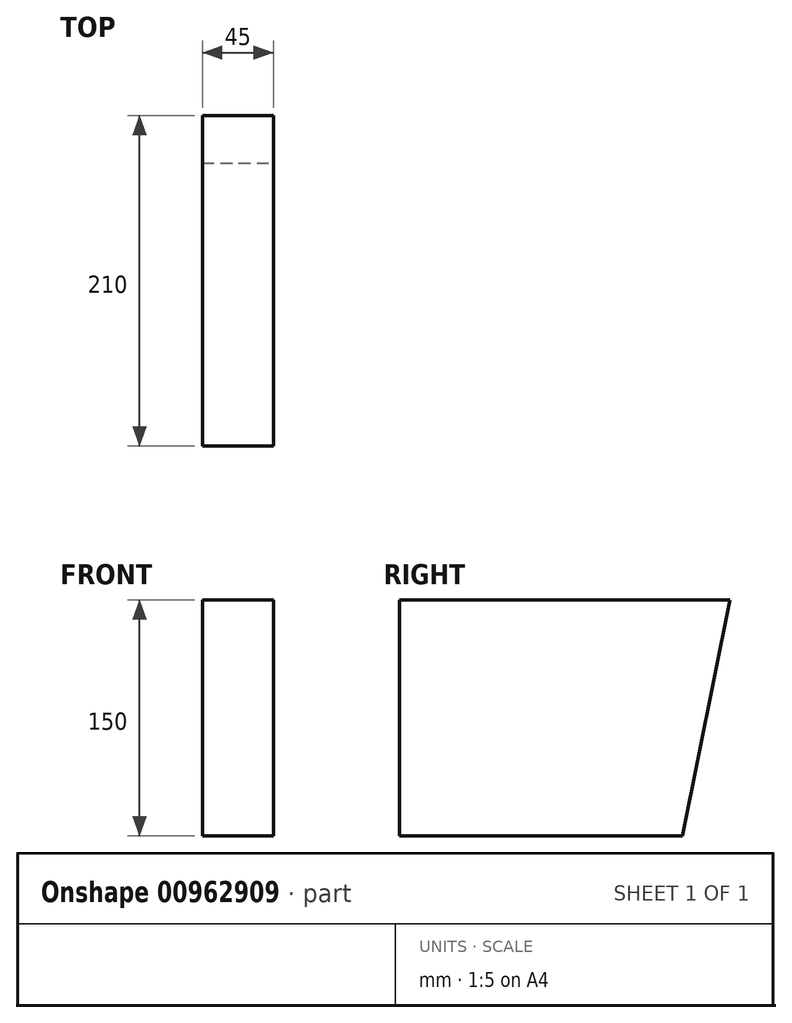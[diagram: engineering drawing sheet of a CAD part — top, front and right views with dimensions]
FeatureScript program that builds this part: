
annotation { "Feature Type Name" : "Feature", "Feature Type Description" : "" }
export const myFeature = defineFeature(function(context is Context, id is Id, definition is map)
    precondition{}
    {
        {
            var Q0;
            Q0=qCreatedBy(makeId("Right.planeOp"),FACE);
            var sketch = newSketch(context, id + "F0", { "sketchPlane" : qUnion([Q0])});
            skLineSegment(sketch, "E0.bottom", {"start": v(-105, 75) * mm, "end": v(105, 75) * mm});
            skLineSegment(sketch, "E0.top", {"start": v(-105, -75) * mm, "end": v(105, -75) * mm});
            skLineSegment(sketch, "E0.left", {"start": v(-105, 75) * mm, "end": v(-105, -75) * mm});
            skLineSegment(sketch, "E0.right", {"start": v(105, 75) * mm, "end": v(105, -75) * mm});
            skPoint(sketch, "E0.middle", {"position": v(0, 0) * mm});
            skSolve(sketch);
        }
        {
            var Q0;
            Q0 = qSketchRegion(id + "F0", true);
            extrude(context, id + "F1", {"entities" : qUnion([Q0]), "depth" : 45 * mm, "offsetDistance" : 25 * mm});
        }
        {
            var Q0;
            Q0=makeQuery(id+"F1.opExtrude","CAP_FACE",FACE,{"disambiguationData":[OSD([sQuery(id+"F0.wireOp",EDGE,"E0.bottom"),sQuery(id+"F0.wireOp",EDGE,"E0.top"),sQuery(id+"F0.wireOp",EDGE,"E0.left"),sQuery(id+"F0.wireOp",EDGE,"E0.right")])],"isStart":false});
            var sketch = newSketch(context, id + "F2", { "sketchPlane" : qUnion([Q0])});
            skLineSegment(sketch, "E1", {"start": v(-105, -75) * mm, "end": v(75, -75) * mm});
            skLineSegment(sketch, "E2", {"start": v(75, -75) * mm, "end": v(105, 75) * mm});
            skSolve(sketch);
        }
        {
            var Q0;
            {var subQ0=sQuery(id+"F2.wireOp",EDGE,"E2");Q0=makeQuery(id+"F2.imprint","IMPRINT",FACE,{"disambiguationData":[TD([[makeQuery(id+"F2.imprint","IMPRINT",EDGE,{"derivedFrom":subQ0}),-1.0]])]});}
            extrude(context, id + "F3", {"entities" : qUnion([Q0]), "operationType" : NewBodyOperationType.REMOVE, "oppositeDirection" : true, "depth" : 69.1 * mm, "offsetDistance" : 25 * mm});
        }
    });
